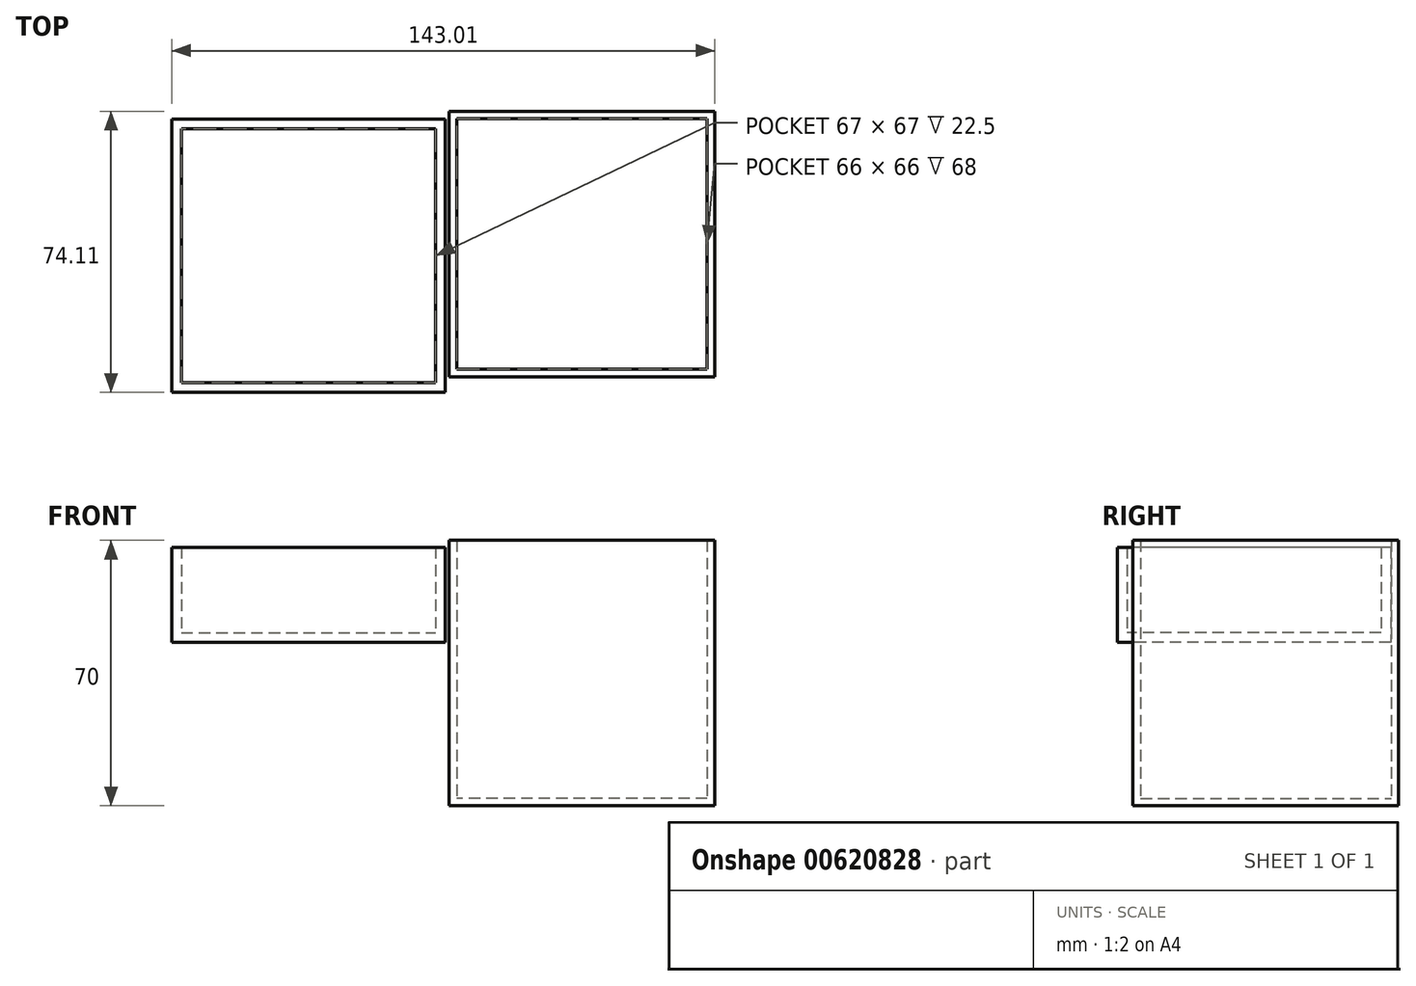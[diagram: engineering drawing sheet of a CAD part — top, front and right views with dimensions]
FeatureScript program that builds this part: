
annotation { "Feature Type Name" : "Feature", "Feature Type Description" : "" }
export const myFeature = defineFeature(function(context is Context, id is Id, definition is map)
    precondition{}
    {
        {
            var Q0;
            Q0=qCreatedBy(makeId("Right.planeOp"),FACE);
            var sketch = newSketch(context, id + "F0", { "sketchPlane" : qUnion([Q0])});
            skLineSegment(sketch, "E0.bottom", {"start": v(-32.28, 26.84) * mm, "end": v(37.72, 26.84) * mm});
            skLineSegment(sketch, "E0.top", {"start": v(-32.28, -43.16) * mm, "end": v(37.72, -43.16) * mm});
            skLineSegment(sketch, "E0.left", {"start": v(-32.28, 26.84) * mm, "end": v(-32.28, -43.16) * mm});
            skLineSegment(sketch, "E0.right", {"start": v(37.72, 26.84) * mm, "end": v(37.72, -43.16) * mm});
            skSolve(sketch);
        }
        {
            var Q0;
            Q0=makeQuery(id+"F0.imprint","IMPRINT",FACE,{"disambiguationData":[TD([[makeQuery(id+"F0.imprint","IMPRINT",EDGE,{"derivedFrom":sQuery(id+"F0.wireOp",EDGE,"E0.bottom")}),-1.0]])]});
            extrude(context, id + "F1", {"entities" : qUnion([Q0]), "depth" : 70 * mm, "offsetDistance" : 25 * mm});
        }
        {
            var Q0;
            Q0=makeQuery(id+"F1.opExtrude","SWEPT_FACE",FACE,{"disambiguationData":[OSD([sQuery(id+"F0.wireOp",EDGE,"E0.bottom")])]});
            shell(context, id + "F2", {"entities" : qUnion([Q0]), "thickness" : 2 * mm});
        }
        {
            var Q0;
            Q0=qCreatedBy(makeId("Top.planeOp"),FACE);
            var sketch = newSketch(context, id + "F3", { "sketchPlane" : qUnion([Q0])});
            skLineSegment(sketch, "E1.bottom", {"start": v(-73.01, 35.61) * mm, "end": v(-1.01, 35.61) * mm});
            skLineSegment(sketch, "E1.top", {"start": v(-73.01, -36.39) * mm, "end": v(-1.01, -36.39) * mm});
            skLineSegment(sketch, "E1.left", {"start": v(-73.01, 35.61) * mm, "end": v(-73.01, -36.39) * mm});
            skLineSegment(sketch, "E1.right", {"start": v(-1.01, 35.61) * mm, "end": v(-1.01, -36.39) * mm});
            skSolve(sketch);
        }
        {
            var Q0;
            Q0=makeQuery(id+"F3.imprint","IMPRINT",FACE,{"disambiguationData":[TD([[makeQuery(id+"F3.imprint","IMPRINT",EDGE,{"derivedFrom":sQuery(id+"F3.wireOp",EDGE,"E1.bottom")}),-1.0]])]});
            extrude(context, id + "F4", {"entities" : qUnion([Q0]), "depth" : 25 * mm, "offsetDistance" : 25 * mm});
        }
        {
            var Q0;
            Q0=makeQuery(id+"F4.opExtrude","CAP_FACE",FACE,{"disambiguationData":[OSD([sQuery(id+"F3.wireOp",EDGE,"E1.bottom"),sQuery(id+"F3.wireOp",EDGE,"E1.top"),sQuery(id+"F3.wireOp",EDGE,"E1.left"),sQuery(id+"F3.wireOp",EDGE,"E1.right")])],"isStart":false});
            shell(context, id + "F5", {"entities" : qUnion([Q0]), "thickness" : 2.5 * mm});
        }
    });
